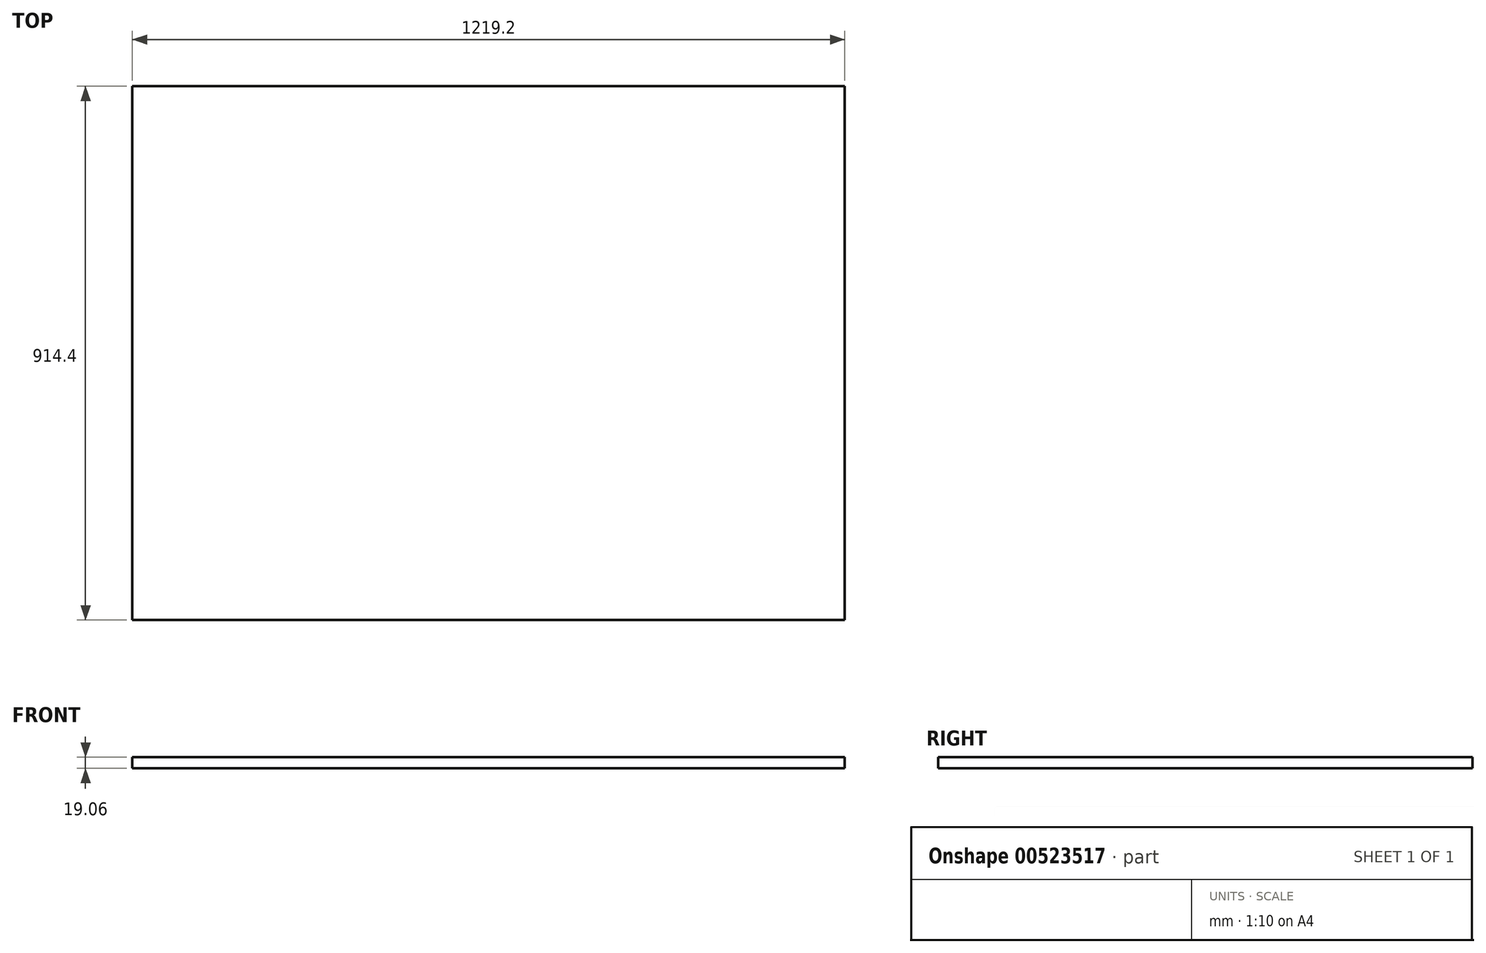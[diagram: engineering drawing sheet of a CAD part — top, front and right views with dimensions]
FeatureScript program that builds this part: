
annotation { "Feature Type Name" : "Feature", "Feature Type Description" : "" }
export const myFeature = defineFeature(function(context is Context, id is Id, definition is map)
    precondition{}
    {
        {
            var Q0;
            Q0=qCreatedBy(makeId("Top.planeOp"),FACE);
            var sketch = newSketch(context, id + "F0", { "sketchPlane" : qUnion([Q0])});
            skLineSegment(sketch, "E0.bottom", {"start": v(-609.6, 457.2) * mm, "end": v(609.6, 457.2) * mm});
            skLineSegment(sketch, "E0.top", {"start": v(-609.6, -457.2) * mm, "end": v(609.6, -457.2) * mm});
            skLineSegment(sketch, "E0.left", {"start": v(-609.6, 457.2) * mm, "end": v(-609.6, -457.2) * mm});
            skLineSegment(sketch, "E0.right", {"start": v(609.6, 457.2) * mm, "end": v(609.6, -457.2) * mm});
            skPoint(sketch, "E0.middle", {"position": v(0, 0) * mm});
            skSolve(sketch);
        }
        {
            var Q0;
            Q0=makeQuery(id+"F0.imprint","IMPRINT",FACE,{"disambiguationData":[TD([[makeQuery(id+"F0.imprint","IMPRINT",EDGE,{"derivedFrom":sQuery(id+"F0.wireOp",EDGE,"E0.bottom")}),-1.0]])]});
            extrude(context, id + "F1", {"entities" : qUnion([Q0]), "endBound" : BoundingType.SYMMETRIC, "depth" : 19.05 * mm, "offsetDistance" : 25.4 * mm});
        }
    });
